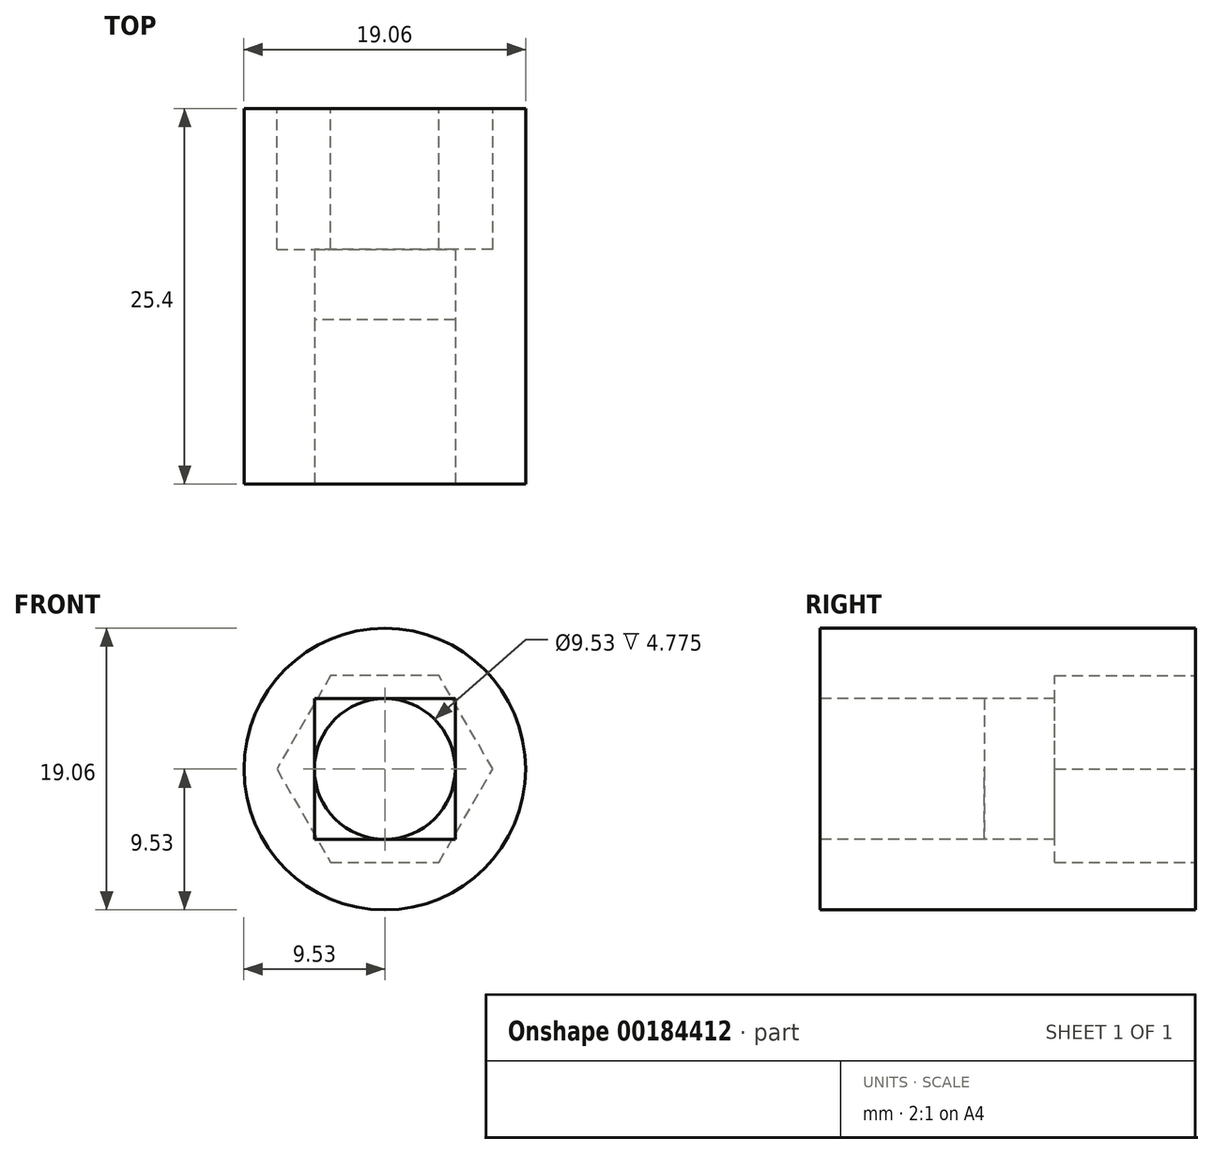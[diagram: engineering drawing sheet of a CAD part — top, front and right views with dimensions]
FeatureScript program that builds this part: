
annotation { "Feature Type Name" : "Feature", "Feature Type Description" : "" }
export const myFeature = defineFeature(function(context is Context, id is Id, definition is map)
    precondition{}
    {
        {
            var Q0;
            Q0=qCreatedBy(makeId("Front.planeOp"),FACE);
            var sketch = newSketch(context, id + "F0", { "sketchPlane" : qUnion([Q0])});
            skCircle(sketch, "E0", {"center": v(0, 0) * mm, "radius": 9.53 * mm});
            skSolve(sketch);
        }
        {
            var Q0;
            Q0 = qSketchRegion(id + "F0", true);
            extrude(context, id + "F1", {"entities" : qUnion([Q0]), "oppositeDirection" : true, "depth" : 25.4 * mm});
        }
        {
            var Q0;
            Q0=qCreatedBy(makeId("Front.planeOp"),FACE);
            var sketch = newSketch(context, id + "F2", { "sketchPlane" : qUnion([Q0])});
            skLineSegment(sketch, "E1.bottom", {"start": v(4.76, 4.76) * mm, "end": v(-4.76, 4.76) * mm});
            skLineSegment(sketch, "E1.top", {"start": v(4.76, -4.76) * mm, "end": v(-4.76, -4.76) * mm});
            skLineSegment(sketch, "E1.left", {"start": v(4.76, 4.76) * mm, "end": v(4.76, -4.76) * mm});
            skLineSegment(sketch, "E1.right", {"start": v(-4.76, 4.76) * mm, "end": v(-4.76, -4.76) * mm});
            skPoint(sketch, "E1.middle", {"position": v(0, 0) * mm});
            skCircle(sketch, "E2", {"center": v(0, 0) * mm, "radius": 4.76 * mm});
            skSolve(sketch);
        }
        {
            var Q0;
            {var subQ0=sQuery(id+"F2.wireOp",EDGE,"E2");var subQ1=makeQuery(id+"F2.imprint","INTERSECT",VERTEX,{"derivedFrom":[sQuery(id+"F2.wireOp",EDGE,"E1.bottom"),subQ0]});Q0=makeQuery(id+"F2.imprint","IMPRINT",FACE,{"disambiguationData":[TD([[makeQuery(id+"F2.imprint","IMPRINT",EDGE,{"disambiguationData":[TD([[subQ1,1.0]])],"derivedFrom":subQ0}),1.0]])]});}
            extrude(context, id + "F3", {"entities" : qUnion([Q0]), "operationType" : NewBodyOperationType.REMOVE, "endBound" : BoundingType.THROUGH_ALL, "oppositeDirection" : true, "depth" : 25.4 * mm});
        }
        {
            var Q0;
            Q0 = qSketchRegion(id + "F2", true);
            extrude(context, id + "F4", {"entities" : qUnion([Q0]), "operationType" : NewBodyOperationType.REMOVE, "oppositeDirection" : true, "depth" : 11.1 * mm});
        }
        {
            var Q0;
            Q0=makeQuery(id+"F1.opExtrude","CAP_FACE",FACE,{"disambiguationData":[OSD([sQuery(id+"F0.wireOp",EDGE,"E0")])],"isStart":false});
            var sketch = newSketch(context, id + "F5", { "sketchPlane" : qUnion([Q0])});
            skCircle(sketch, "E3.cCircle", {"center": v(0, 0) * mm, "radius": 6.32 * mm, "construction": true});
            skLineSegment(sketch, "E3.0", {"start": v(-3.65, 6.32) * mm, "end": v(3.65, 6.32) * mm});
            skLineSegment(sketch, "E3.1", {"start": v(3.65, 6.32) * mm, "end": v(7.3, 0) * mm});
            skLineSegment(sketch, "E3.2", {"start": v(7.3, 0) * mm, "end": v(3.65, -6.32) * mm});
            skLineSegment(sketch, "E3.3", {"start": v(3.65, -6.32) * mm, "end": v(-3.65, -6.32) * mm});
            skLineSegment(sketch, "E3.4", {"start": v(-3.65, -6.32) * mm, "end": v(-7.3, 0) * mm});
            skLineSegment(sketch, "E3.5", {"start": v(-7.3, 0) * mm, "end": v(-3.65, 6.32) * mm});
            skPoint(sketch, "E3.0.midPoint", {"position": v(0, 6.32) * mm});
            skSolve(sketch);
        }
        {
            var Q0;
            Q0=makeQuery(id+"F5.imprint","IMPRINT",FACE,{"disambiguationData":[TD([[makeQuery(id+"F5.imprint","IMPRINT",EDGE,{"derivedFrom":sQuery(id+"F5.wireOp",EDGE,"E3.0")}),-1.0]])]});
            extrude(context, id + "F6", {"entities" : qUnion([Q0]), "operationType" : NewBodyOperationType.REMOVE, "oppositeDirection" : true, "depth" : 9.52 * mm});
        }
    });
